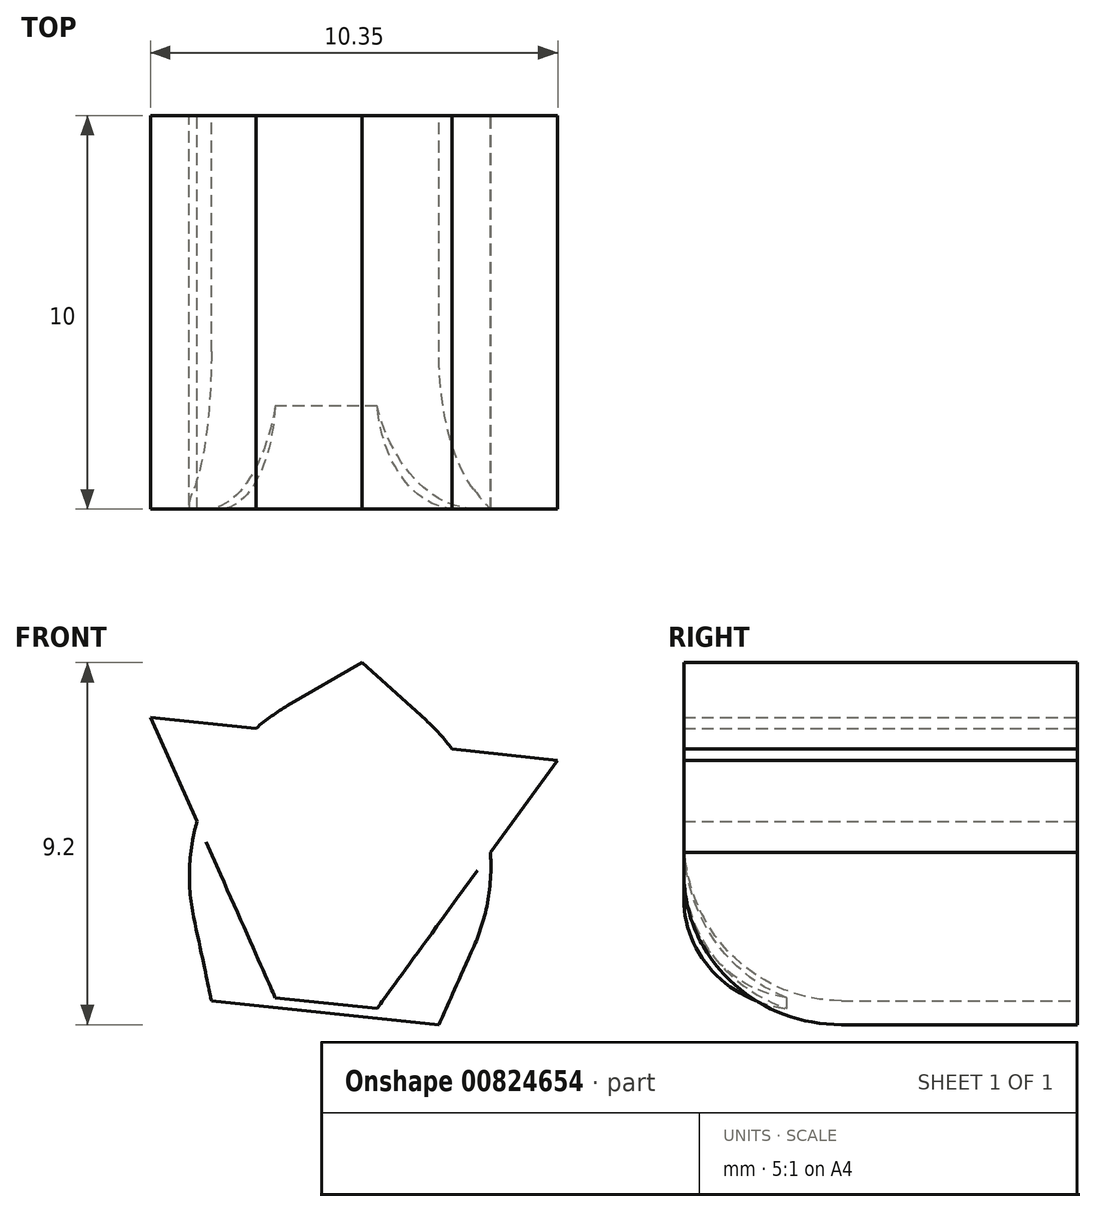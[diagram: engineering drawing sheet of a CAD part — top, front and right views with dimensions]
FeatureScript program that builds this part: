
annotation { "Feature Type Name" : "Feature", "Feature Type Description" : "" }
export const myFeature = defineFeature(function(context is Context, id is Id, definition is map)
    precondition{}
    {
        {
            var Q0;
            Q0=qCreatedBy(makeId("Front.planeOp"),FACE);
            var sketch = newSketch(context, id + "F0", { "sketchPlane" : qUnion([Q0])});
            skCircle(sketch, "E0.cCircle", {"center": v(0, 0) * mm, "radius": 4 * mm, "construction": true});
            skLineSegment(sketch, "E0.0", {"start": v(0.52, 4.92) * mm, "end": v(4.84, 1.03) * mm});
            skLineSegment(sketch, "E0.1", {"start": v(4.84, 1.03) * mm, "end": v(2.47, -4.28) * mm});
            skLineSegment(sketch, "E0.2", {"start": v(2.47, -4.28) * mm, "end": v(-3.31, -3.67) * mm});
            skLineSegment(sketch, "E0.3", {"start": v(-3.31, -3.67) * mm, "end": v(-4.52, 2.01) * mm});
            skLineSegment(sketch, "E0.4", {"start": v(-4.52, 2.01) * mm, "end": v(0.52, 4.92) * mm});
            skPoint(sketch, "E0.0.midPoint", {"position": v(2.68, 2.97) * mm});
            skSolve(sketch);
        }
        {
            var Q0;
            Q0=makeQuery(id+"F0.imprint","IMPRINT",FACE,{"disambiguationData":[TD([[makeQuery(id+"F0.imprint","IMPRINT",EDGE,{"derivedFrom":sQuery(id+"F0.wireOp",EDGE,"E0.0")}),-1.0]])]});
            extrude(context, id + "F1", {"entities" : qUnion([Q0]), "depth" : 10 * mm, "offsetDistance" : 25 * mm});
        }
        {
            var Q0;
            Q0=makeQuery(id+"F1.opExtrude","CAP_EDGE",EDGE,{"disambiguationData":[OSD([sQuery(id+"F0.wireOp",EDGE,"E0.2")])],"isStart":false});
            fillet(context, id + "F2", {"entities" : qUnion([Q0]), "radius" : 4 * mm, "tangentPropagation" : true, "allowEdgeOverflow" : false});
        }
        {
            var Q0;
            Q0=makeQuery(id+"F1.opExtrude","SWEPT_EDGE",EDGE,{"disambiguationData":[OSD([sQuery(id+"F0.wireOp",EDGE,"E0.0"),sQuery(id+"F0.wireOp",EDGE,"E0.1")])]});
            fillet(context, id + "F3", {"entities" : qUnion([Q0]), "radius" : 5 * mm, "tangentPropagation" : true, "allowEdgeOverflow" : false});
        }
        {
            var Q0;
            Q0=makeQuery(id+"F1.opExtrude","SWEPT_EDGE",EDGE,{"disambiguationData":[OSD([sQuery(id+"F0.wireOp",EDGE,"E0.3"),sQuery(id+"F0.wireOp",EDGE,"E0.4")])]});
            fillet(context, id + "F4", {"entities" : qUnion([Q0]), "radius" : 5 * mm, "tangentPropagation" : true, "allowEdgeOverflow" : false});
        }
        {
            var Q0;
            Q0=qCreatedBy(makeId("Front.planeOp"),FACE);
            var sketch = newSketch(context, id + "F5", { "sketchPlane" : qUnion([Q0])});
            skCircle(sketch, "E1.cCircle", {"center": v(0, 0) * mm, "radius": 3 * mm, "construction": true});
            skLineSegment(sketch, "E1.0", {"start": v(-4.86, 3.53) * mm, "end": v(5.49, 2.44) * mm});
            skLineSegment(sketch, "E1.1", {"start": v(5.49, 2.44) * mm, "end": v(-0.63, -5.97) * mm});
            skLineSegment(sketch, "E1.2", {"start": v(-0.63, -5.97) * mm, "end": v(-4.86, 3.53) * mm});
            skPoint(sketch, "E1.0.midPoint", {"position": v(0.32, 2.99) * mm});
            skSolve(sketch);
        }
        {
            var Q0;
            Q0=makeQuery(id+"F5.imprint","IMPRINT",FACE,{"disambiguationData":[TD([[makeQuery(id+"F5.imprint","IMPRINT",EDGE,{"derivedFrom":sQuery(id+"F5.wireOp",EDGE,"E1.0")}),-1.0]])]});
            extrude(context, id + "F6", {"entities" : qUnion([Q0]), "operationType" : NewBodyOperationType.ADD, "depth" : 10 * mm, "offsetDistance" : 25 * mm});
        }
        {
            var Q0;
            Q0=makeQuery(id+"F6.opExtrude","SWEPT_EDGE",EDGE,{"disambiguationData":[OSD([sQuery(id+"F5.wireOp",EDGE,"E1.1"),sQuery(id+"F5.wireOp",EDGE,"E1.2")])]});
            chamfer(context, id + "F7", {"entities" : qUnion([Q0]), "width" : 1.5 * mm, "tangentPropagation" : true});
        }
        {
            var Q0;
            {var subQ0=sQuery(id+"F5.wireOp",EDGE,"E1.2");var subQ1=sQuery(id+"F5.wireOp",EDGE,"E1.1");Q0=makeQuery(id+"F7.opChamfer","BLEND_EDGE",EDGE,{"blendedFrom":[makeQuery(id+"F6.opExtrude","SWEPT_EDGE",EDGE,{"disambiguationData":[OSD([subQ1,subQ0])]}),makeQuery(id+"F6.boolean.opBoolean","MERGE",FACE,{"derivedFrom":[makeQuery(id+"F1.opExtrude","CAP_FACE",FACE,{"disambiguationData":[OSD([sQuery(id+"F0.wireOp",EDGE,"E0.0"),sQuery(id+"F0.wireOp",EDGE,"E0.1"),sQuery(id+"F0.wireOp",EDGE,"E0.2"),sQuery(id+"F0.wireOp",EDGE,"E0.3"),sQuery(id+"F0.wireOp",EDGE,"E0.4")])],"isStart":false}),makeQuery(id+"F6.opExtrude","CAP_FACE",FACE,{"disambiguationData":[OSD([sQuery(id+"F5.wireOp",EDGE,"E1.0"),subQ1,subQ0])],"isStart":false})]})],"blendedInto":[makeQuery(id+"F6.boolean.opBoolean","MERGE",FACE,{"derivedFrom":[makeQuery(id+"F1.opExtrude","CAP_FACE",FACE,{"disambiguationData":[OSD([sQuery(id+"F0.wireOp",EDGE,"E0.0"),sQuery(id+"F0.wireOp",EDGE,"E0.1"),sQuery(id+"F0.wireOp",EDGE,"E0.2"),sQuery(id+"F0.wireOp",EDGE,"E0.3"),sQuery(id+"F0.wireOp",EDGE,"E0.4")])],"isStart":false}),makeQuery(id+"F6.opExtrude","CAP_FACE",FACE,{"disambiguationData":[OSD([sQuery(id+"F5.wireOp",EDGE,"E1.0"),subQ1,subQ0])],"isStart":false})]})]});}
            fillet(context, id + "F8", {"entities" : qUnion([Q0]), "radius" : 3 * mm, "tangentPropagation" : true, "allowEdgeOverflow" : false});
        }
    });
